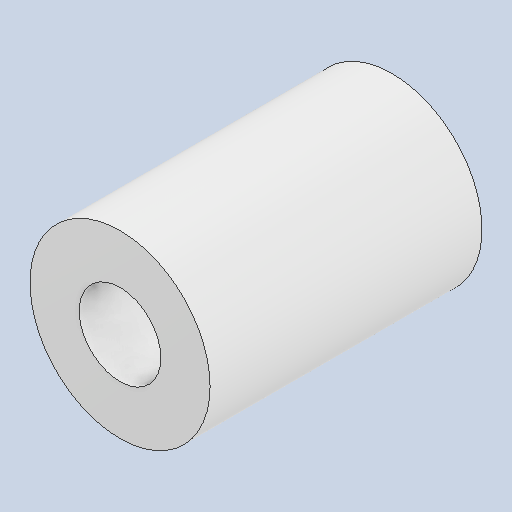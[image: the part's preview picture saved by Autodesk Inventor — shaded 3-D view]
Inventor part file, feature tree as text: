
AUTODESK INVENTOR PART (.ipt)
format: ipt  version: 2023 (Build 270158000, 158)  size: 102,912 bytes
history: native  units: in
note: dims shown in document units (in); Inventor stores cm internally (conversion verified against a paired STEP export)
features: other x3, sketch x1, plane x1
ambient origin geometry x8: Origin, YZ Plane, XZ Plane, XY Plane, X Axis, Y Axis, Z Axis, Center Point
bodies: Solid1 (feature_tree)
feature tree (5):
  other  "IntakeBearingSpacer.ipt"
  other  "Solid1::IntakeBearingSpacer.ipt"
  other  "TaggingFeature1"
  sketch  "Sketch1"  dims[d0=0.3937in]
  plane  "Work Plane1"
